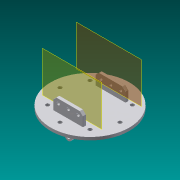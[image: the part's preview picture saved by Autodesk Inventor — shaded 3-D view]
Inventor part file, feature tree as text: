
AUTODESK INVENTOR PART (.ipt)
format: ipt  version: 2013 SP2 (Build 170200200, 200)  size: 337,920 bytes
history: native  units: in
note: dims shown in document units (in); Inventor stores cm internally (conversion verified against a paired STEP export)
features: sketch x9, extrude x7, fillet x6, projected_geometry x4, reference x3, plane x2
ambient origin geometry x8: Origin, YZ Plane, XZ Plane, XY Plane, X Axis, Y Axis, Z Axis, Center Point
bodies: Solid1 (feature_tree)
feature tree (31):
  plane  "Work Plane1"
  extrude  "Extrusion1"  Depth=0.0938in TaperAngle=0.0deg
  fillet  "Fillet1"  Radius=0.01in
  fillet  "Fillet2"  Radius=0.01in
  fillet  "Fillet3"  Radius=0.01in
  fillet  "Fillet4"  Radius=0.01in
  fillet  "Fillet5"  Radius=0.01in
  extrude  "Extrusion2"  Depth=0.0938in TaperAngle=0.0deg
  extrude  "Extrusion3"  Depth=0.118in
  plane  "Work Plane2"
  extrude  "Extrusion4"  Depth=0.118in
  fillet  "Fillet6"  Radius=0.118in
  extrude  "Extrusion5"  Depth=0.118in
  extrude  "Extrusion6"  Depth=4.0in TaperAngle=0.0deg
  extrude  "Extrusion7"  Depth=0.01in
  sketch  "Sketch8"  dims[d34=0.118in]
  sketch  "Sketch9"  dims[d35=0.228in d36=0.0938in d37=0.0in d38=0.0938in d39=0.0in d40=0.0938in d41=0.0in]
  sketch  "Sketch1"  dims[d2=0.123in d7=0.0938in d8=0.0in d9=0.01in d10=0.01in d11=0.01in d12=0.01in d13=0.01in]
  reference  "Reference1"
  sketch  "Sketch2"  dims[d14=2.5in d15=0.0938in d16=0.0in]
  reference  "Reference2"
  reference  "Reference3"
  sketch  "Sketch3"  dims[d18=0.118in d21=0.118in]
  projected_geometry  "Projected Loop1"
  sketch  "Sketch4"  dims[d22=0.118in d23=0.118in d24=0.118in]
  projected_geometry  "Projected Loop2"
  sketch  "Sketch5"  dims[d25=0.118in d26=0.118in]
  projected_geometry  "Projected Loop3"
  sketch  "Sketch6"  dims[d27=0.118in d28=4.0in d29=0.0in]
  projected_geometry  "Projected Loop4"
  sketch  "Sketch7"  dims[d30=0.0938in d31=0.0in d32=0.01in]
